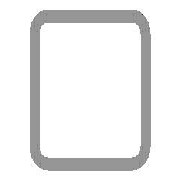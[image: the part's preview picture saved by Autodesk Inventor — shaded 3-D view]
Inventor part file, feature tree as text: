
AUTODESK INVENTOR PART (.ipt)
format: ipt  version: 2022 (Build 260153000, 153)  size: 651,264 bytes
history: native  units: mm (DEFAULTED — no unit token found)
features: other x8, sketch x5, plane x2, hole x2, surface_op x2, split x1
ambient origin geometry x8: Origin, YZ Plane, XZ Plane, XY Plane, X Axis, Y Axis, Z Axis, Center Point
bodies: Solid1 (feature_tree), Body (feature_tree), Solid7 (feature_tree), Solid8 (feature_tree)
feature tree (20):
  parser-record x1  (decoder bookkeeping rows leaked as tree rows — omitted from the tree; the rows remain in map.json)
  other  "Driven Length"
  other  "Start Plane"
  other  "End Plane"
  plane  "Work Plane4"
  split  "Split1"
  hole  "Hole1"  [1 undecoded]
  hole  "Hole2"  [1 undecoded]
  sketch  "Sketch"  dims[d13=-20.0mm d14=430.0mm d15=20.0mm d16=20.0mm d17=90.0deg d18=450.0mm d55=5.0mm d56=5.0mm d57=5.0mm d58=5.0mm d59=5.0mm d60=5.0mm d61=5.0mm d62=5.0mm d63=0.0mm d64=5.0mm d65=5.0mm d66=5.0mm d67=5.0mm d68=5.0mm d69=5.0mm d70=5.0mm d71=5.0mm d72=0.0mm d73=6.6mm d74=6.0mm d75=4.0mm d76=2.0mm d77=90.0deg d78=8.0mm d79=0.0mm d80=6.6mm d81=6.0mm d82=4.0mm d83=2.0mm d84=90.0deg d85=8.0mm d86=0.0mm]
  sketch  "Sketch3"  dims[d3=437.5mm d4=0.0mm]
  plane  "Work Plane3"
  sketch  "Sketch4"  dims[d7=4.0mm d9=40.0mm]
  other  "Srf12"
  other  "Srf13"
  sketch  "Sketch5"  dims[d11=40.0mm]
  sketch  "Sketch6"  dims[d12=2.0mm]
  other  "Srf10"
  other  "Srf11"
  surface_op  "Boundary Patch5"
  surface_op  "Boundary Patch6"
note: 2 required parameter values undecoded (feature->parameter linkage not recoverable at this tier; creation-order binding heuristic only, values carry confidence <= 0.55)
